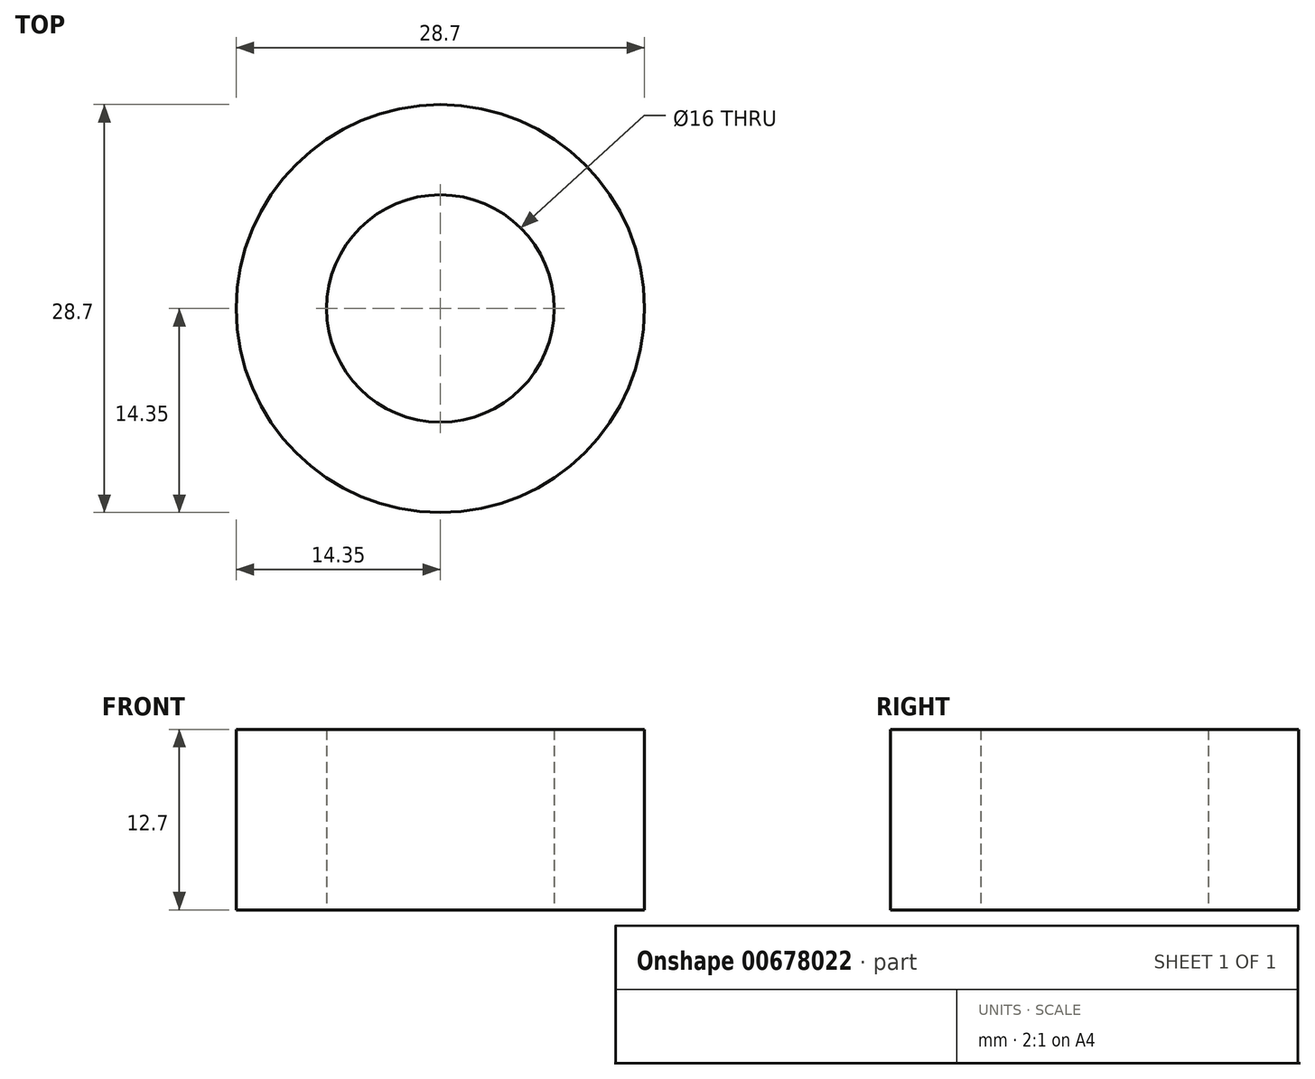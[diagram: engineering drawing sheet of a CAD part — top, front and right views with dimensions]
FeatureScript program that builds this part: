
annotation { "Feature Type Name" : "Feature", "Feature Type Description" : "" }
export const myFeature = defineFeature(function(context is Context, id is Id, definition is map)
    precondition{}
    {
        {
            var Q0;
            Q0=qCreatedBy(makeId("Top.planeOp"),FACE);
            var sketch = newSketch(context, id + "F0", { "sketchPlane" : qUnion([Q0])});
            skCircle(sketch, "E0", {"center": v(0, 0) * mm, "radius": 8 * mm});
            skCircle(sketch, "E1.0", {"center": v(0, 0) * mm, "radius": 14.35 * mm});
            skSolve(sketch);
        }
        {
            var Q0;
            Q0=makeQuery(id+"F0.imprint","IMPRINT",FACE,{"disambiguationData":[TD([[makeQuery(id+"F0.imprint","IMPRINT",EDGE,{"derivedFrom":sQuery(id+"F0.wireOp",EDGE,"E0")}),-1.0]])]});
            extrude(context, id + "F1", {"entities" : qUnion([Q0]), "depth" : 12.7 * mm, "offsetDistance" : 25.4 * mm});
        }
    });
